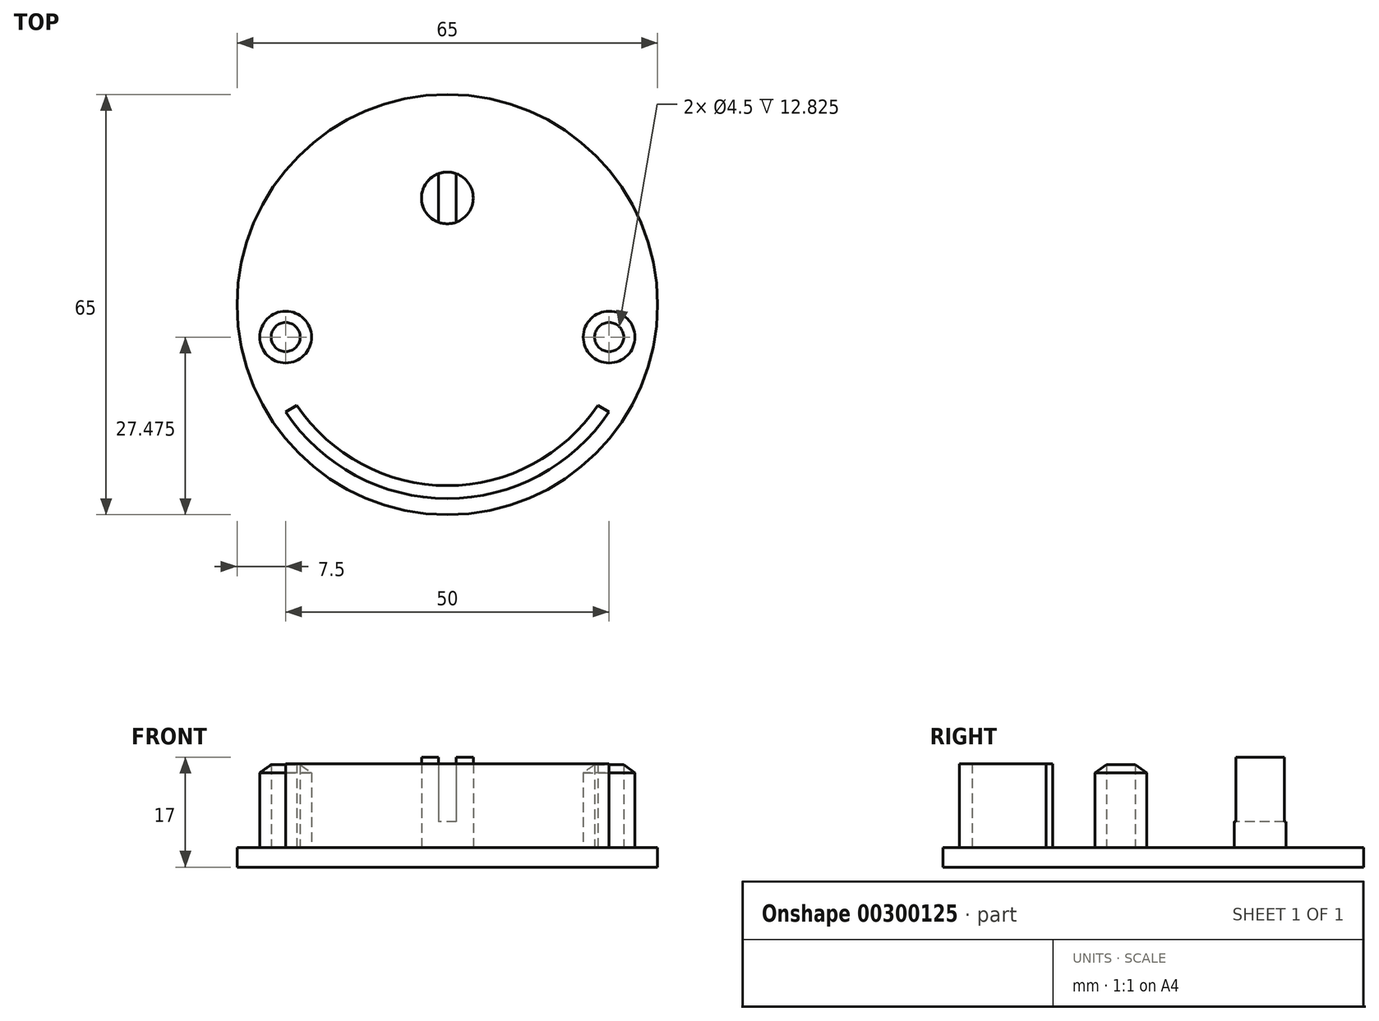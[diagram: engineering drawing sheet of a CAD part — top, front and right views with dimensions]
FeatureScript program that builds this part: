
annotation { "Feature Type Name" : "Feature", "Feature Type Description" : "" }
export const myFeature = defineFeature(function(context is Context, id is Id, definition is map)
    precondition{}
    {
        {
            var Q0;
            Q0=qCreatedBy(makeId("Top.planeOp"),FACE);
            var sketch = newSketch(context, id + "F0", { "sketchPlane" : qUnion([Q0])});
            skCircle(sketch, "E0", {"center": v(0, 0) * mm, "radius": 32.5 * mm});
            skArc(sketch, "E1", {"start": v(-25, -16.58) * mm, "mid": v(0, -30) * mm, "end": v(25, -16.58) * mm});
            skArc(sketch, "E2", {"start": v(-23.26, -15.58) * mm, "mid": v(0, -28) * mm, "end": v(23.26, -15.58) * mm});
            skLineSegment(sketch, "E3", {"start": v(25, -16.58) * mm, "end": v(23.26, -15.58) * mm});
            skLineSegment(sketch, "E4", {"start": v(-25, -16.58) * mm, "end": v(-23.26, -15.58) * mm});
            skLineSegment(sketch, "E5", {"start": v(23.26, -15.58) * mm, "end": v(-23.26, -15.58) * mm});
            skCircle(sketch, "E6", {"center": v(25, -5.02) * mm, "radius": 4 * mm});
            skCircle(sketch, "E7", {"center": v(-25, -5.02) * mm, "radius": 4 * mm});
            skCircle(sketch, "E8", {"center": v(-25, -5.02) * mm, "radius": 2.25 * mm});
            skCircle(sketch, "E9", {"center": v(25, -5.02) * mm, "radius": 2.25 * mm});
            skCircle(sketch, "E10", {"center": v(0, 16.5) * mm, "radius": 4 * mm});
            skLineSegment(sketch, "E11", {"start": v(1.38, 20.26) * mm, "end": v(1.38, 12.74) * mm});
            skLineSegment(sketch, "E12", {"start": v(-1.38, 20.26) * mm, "end": v(-1.38, 12.74) * mm});
            skSolve(sketch);
        }
        {
            var Q0;
            Q0=makeQuery(id+"F0.imprint","IMPRINT",FACE,{"disambiguationData":[TD([[makeQuery(id+"F0.imprint","IMPRINT",EDGE,{"derivedFrom":sQuery(id+"F0.wireOp",EDGE,"E0")}),1.0]])]});
            var Q1;
            {var subQ0=sQuery(id+"F0.wireOp",EDGE,"E11");Q1=makeQuery(id+"F0.imprint","IMPRINT",FACE,{"disambiguationData":[TD([[makeQuery(id+"F0.imprint","IMPRINT",EDGE,{"derivedFrom":subQ0}),-1.0]])]});}
            var Q2;
            {var subQ0=sQuery(id+"F0.wireOp",EDGE,"E11");Q2=makeQuery(id+"F0.imprint","IMPRINT",FACE,{"disambiguationData":[TD([[makeQuery(id+"F0.imprint","IMPRINT",EDGE,{"derivedFrom":subQ0}),1.0]])]});}
            var Q3;
            {var subQ0=sQuery(id+"F0.wireOp",EDGE,"E12");Q3=makeQuery(id+"F0.imprint","IMPRINT",FACE,{"disambiguationData":[TD([[makeQuery(id+"F0.imprint","IMPRINT",EDGE,{"derivedFrom":subQ0}),-1.0]])]});}
            var Q4;
            Q4=makeQuery(id+"F0.imprint","IMPRINT",FACE,{"disambiguationData":[TD([[makeQuery(id+"F0.imprint","IMPRINT",EDGE,{"derivedFrom":sQuery(id+"F0.wireOp",EDGE,"E6")}),1.0]])]});
            var Q5;
            Q5=makeQuery(id+"F0.imprint","IMPRINT",FACE,{"disambiguationData":[TD([[makeQuery(id+"F0.imprint","IMPRINT",EDGE,{"derivedFrom":sQuery(id+"F0.wireOp",EDGE,"E9")}),1.0]])]});
            var Q6;
            Q6=makeQuery(id+"F0.imprint","IMPRINT",FACE,{"disambiguationData":[TD([[makeQuery(id+"F0.imprint","IMPRINT",EDGE,{"derivedFrom":sQuery(id+"F0.wireOp",EDGE,"E8")}),1.0]])]});
            var Q7;
            Q7=makeQuery(id+"F0.imprint","IMPRINT",FACE,{"disambiguationData":[TD([[makeQuery(id+"F0.imprint","IMPRINT",EDGE,{"derivedFrom":sQuery(id+"F0.wireOp",EDGE,"E7")}),1.0]])]});
            var Q8;
            Q8=makeQuery(id+"F0.imprint","IMPRINT",FACE,{"disambiguationData":[TD([[makeQuery(id+"F0.imprint","IMPRINT",EDGE,{"derivedFrom":sQuery(id+"F0.wireOp",EDGE,"E1")}),1.0]])]});
            var Q9;
            Q9=makeQuery(id+"F0.imprint","IMPRINT",FACE,{"disambiguationData":[TD([[makeQuery(id+"F0.imprint","IMPRINT",EDGE,{"derivedFrom":sQuery(id+"F0.wireOp",EDGE,"E2")}),1.0]])]});
            extrude(context, id + "F1", {"entities" : qUnion([Q0, Q1, Q2, Q3, Q4, Q5, Q6, Q7, Q8, Q9]), "depth" : 3 * mm});
        }
        {
            var Q0;
            Q0=makeQuery(id+"F0.imprint","IMPRINT",FACE,{"disambiguationData":[TD([[makeQuery(id+"F0.imprint","IMPRINT",EDGE,{"derivedFrom":sQuery(id+"F0.wireOp",EDGE,"E1")}),1.0]])]});
            extrude(context, id + "F2", {"entities" : qUnion([Q0]), "operationType" : NewBodyOperationType.ADD, "depth" : 16 * mm, "hasSecondDirection" : true, "secondDirectionOppositeDirection" : false, "secondDirectionDepth" : 3 * mm});
        }
        {
            var Q0;
            Q0=makeQuery(id+"F0.imprint","IMPRINT",FACE,{"disambiguationData":[TD([[makeQuery(id+"F0.imprint","IMPRINT",EDGE,{"derivedFrom":sQuery(id+"F0.wireOp",EDGE,"E7")}),1.0]])]});
            var Q1;
            Q1=makeQuery(id+"F0.imprint","IMPRINT",FACE,{"disambiguationData":[TD([[makeQuery(id+"F0.imprint","IMPRINT",EDGE,{"derivedFrom":sQuery(id+"F0.wireOp",EDGE,"E6")}),1.0]])]});
            var Q2;
            Q2=sQuery(id+"F0.wireOp",EDGE,"E7");
            var Q3;
            Q3=sQuery(id+"F0.wireOp",EDGE,"E8");
            var Q4;
            Q4=sQuery(id+"F0.wireOp",EDGE,"E9");
            var Q5;
            Q5=sQuery(id+"F0.wireOp",EDGE,"E6");
            extrude(context, id + "F3", {"entities" : qUnion([Q0, Q1]), "operationType" : NewBodyOperationType.ADD, "surfaceEntities" : qUnion([Q2, Q3, Q4, Q5]), "depth" : 16 * mm, "hasSecondDirection" : true, "secondDirectionOppositeDirection" : false, "secondDirectionDepth" : 3 * mm});
        }
        {
            var Q0;
            Q0=makeQuery(id+"F3.opExtrude","CAP_EDGE",EDGE,{"disambiguationData":[OSD([sQuery(id+"F0.wireOp",EDGE,"E7")])],"isStart":false});
            var Q1;
            Q1=makeQuery(id+"F3.opExtrude","CAP_EDGE",EDGE,{"disambiguationData":[OSD([sQuery(id+"F0.wireOp",EDGE,"E6")])],"isStart":false});
            chamfer(context, id + "F4", {"entities" : qUnion([Q0, Q1]), "chamferType" : ChamferType.OFFSET_ANGLE, "width" : 2 * mm, "oppositeDirection" : false, "angle" : 35 * degree, "tangentPropagation" : true});
        }
        {
            var Q0;
            {var subQ0=sQuery(id+"F0.wireOp",EDGE,"E11");Q0=makeQuery(id+"F0.imprint","IMPRINT",FACE,{"disambiguationData":[TD([[makeQuery(id+"F0.imprint","IMPRINT",EDGE,{"derivedFrom":subQ0}),1.0]])]});}
            var Q1;
            {var subQ0=sQuery(id+"F0.wireOp",EDGE,"E12");Q1=makeQuery(id+"F0.imprint","IMPRINT",FACE,{"disambiguationData":[TD([[makeQuery(id+"F0.imprint","IMPRINT",EDGE,{"derivedFrom":subQ0}),-1.0]])]});}
            var Q2;
            {var subQ0=sQuery(id+"F0.wireOp",EDGE,"E11");Q2=makeQuery(id+"F0.imprint","IMPRINT",FACE,{"disambiguationData":[TD([[makeQuery(id+"F0.imprint","IMPRINT",EDGE,{"derivedFrom":subQ0}),-1.0]])]});}
            extrude(context, id + "F5", {"entities" : qUnion([Q0, Q1, Q2]), "operationType" : NewBodyOperationType.ADD, "depth" : 7 * mm, "hasSecondDirection" : true, "secondDirectionOppositeDirection" : false, "secondDirectionDepth" : 3 * mm});
        }
        {
            var Q0;
            {var subQ0=sQuery(id+"F0.wireOp",EDGE,"E12");Q0=makeQuery(id+"F0.imprint","IMPRINT",FACE,{"disambiguationData":[TD([[makeQuery(id+"F0.imprint","IMPRINT",EDGE,{"derivedFrom":subQ0}),-1.0]])]});}
            var Q1;
            {var subQ0=sQuery(id+"F0.wireOp",EDGE,"E11");Q1=makeQuery(id+"F0.imprint","IMPRINT",FACE,{"disambiguationData":[TD([[makeQuery(id+"F0.imprint","IMPRINT",EDGE,{"derivedFrom":subQ0}),1.0]])]});}
            extrude(context, id + "F6", {"entities" : qUnion([Q0, Q1]), "operationType" : NewBodyOperationType.ADD, "depth" : 17 * mm, "hasSecondDirection" : true, "secondDirectionOppositeDirection" : false, "secondDirectionDepth" : 7 * mm});
        }
    });
